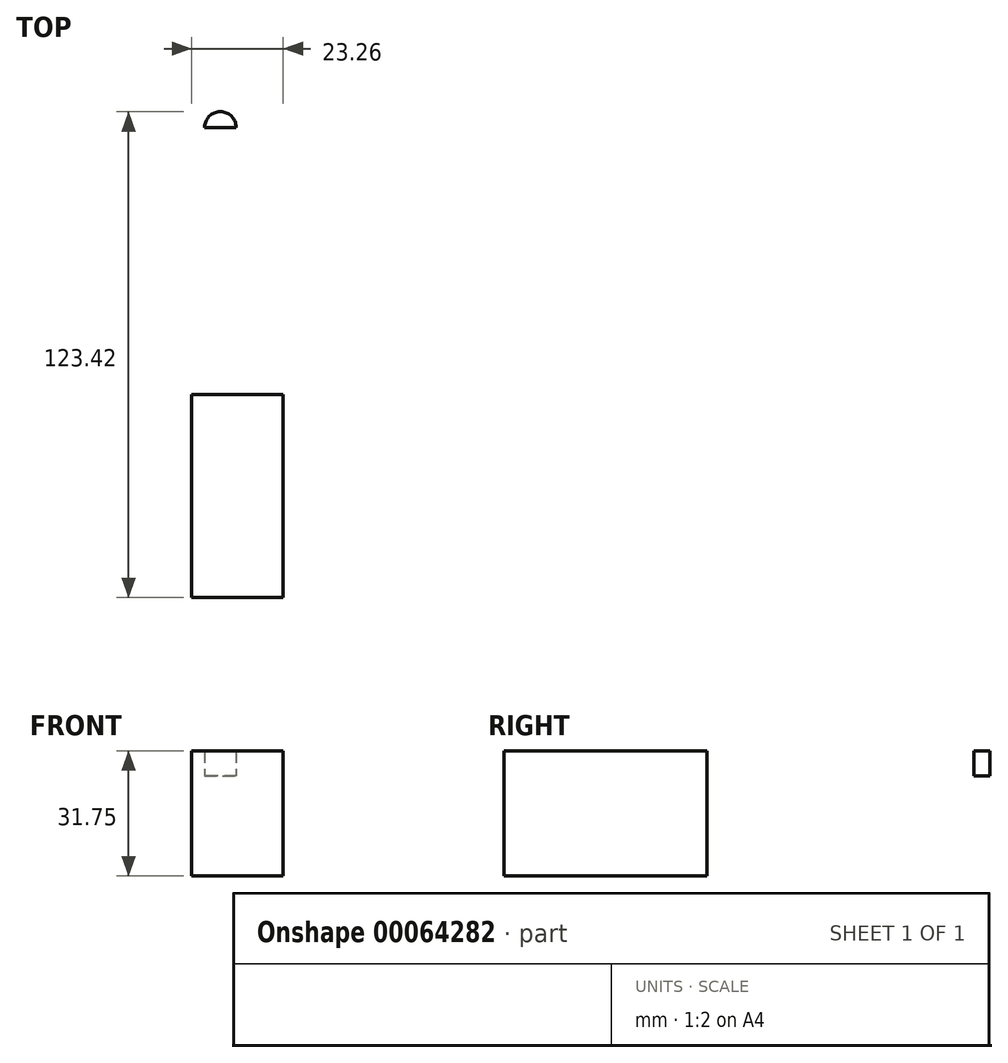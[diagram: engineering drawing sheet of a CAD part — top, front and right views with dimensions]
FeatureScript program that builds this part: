
annotation { "Feature Type Name" : "Feature", "Feature Type Description" : "" }
export const myFeature = defineFeature(function(context is Context, id is Id, definition is map)
    precondition{}
    {
        {
            var Q0;
            Q0=qCreatedBy(makeId("Top.planeOp"),FACE);
            var sketch = newSketch(context, id + "F0", { "sketchPlane" : qUnion([Q0])});
            skLineSegment(sketch, "E0.bottom", {"start": v(-34.6, -75.35) * mm, "end": v(-18.96, -75.35) * mm});
            skLineSegment(sketch, "E0.top", {"start": v(-34.6, -23.79) * mm, "end": v(-18.96, -23.79) * mm});
            skLineSegment(sketch, "E0.left", {"start": v(-34.6, -75.35) * mm, "end": v(-34.6, -23.79) * mm});
            skLineSegment(sketch, "E0.right", {"start": v(-18.96, -75.35) * mm, "end": v(-18.96, -23.79) * mm});
            skLineSegment(sketch, "E1.bottom", {"start": v(-31.27, -23.79) * mm, "end": v(-23.29, -23.79) * mm});
            skLineSegment(sketch, "E1.top", {"start": v(-31.27, 44.08) * mm, "end": v(-23.29, 44.08) * mm});
            skLineSegment(sketch, "E1.left", {"start": v(-31.27, -23.79) * mm, "end": v(-31.27, 44.08) * mm});
            skLineSegment(sketch, "E1.right", {"start": v(-23.29, -23.79) * mm, "end": v(-23.29, 44.08) * mm});
            skArc(sketch, "E2", {"start": v(-23.29, 44.08) * mm, "mid": v(-27.28, 48.07) * mm, "end": v(-31.27, 44.08) * mm});
            skSolve(sketch);
        }
        {
            var Q0;
            Q0=makeQuery(id+"F0.imprint","IMPRINT",FACE,{"disambiguationData":[TD([[makeQuery(id+"F0.imprint","IMPRINT",EDGE,{"derivedFrom":sQuery(id+"F0.wireOp",EDGE,"E1.bottom")}),1.0]])]});
            var Q1;
            Q1=makeQuery(id+"F0.imprint","IMPRINT",FACE,{"disambiguationData":[TD([[makeQuery(id+"F0.imprint","IMPRINT",EDGE,{"derivedFrom":sQuery(id+"F0.wireOp",EDGE,"E1.top")}),1.0]])]});
            var Q2;
            Q2=makeQuery(id+"F0.imprint","IMPRINT",FACE,{"disambiguationData":[TD([[makeQuery(id+"F0.imprint","IMPRINT",EDGE,{"derivedFrom":sQuery(id+"F0.wireOp",EDGE,"E0.bottom")}),1.0]])]});
            extrude(context, id + "F1", {"entities" : qUnion([Q0, Q1, Q2]), "depth" : 6.35 * mm});
        }
        {
            var Q0;
            Q0=makeQuery(id+"F1.opExtrude","SWEPT_FACE",FACE,{"disambiguationData":[OSD([sQuery(id+"F0.wireOp",EDGE,"E0.right")])]});
            extrude(context, id + "F2", {"entities" : qUnion([Q0]), "operationType" : NewBodyOperationType.ADD, "depth" : 7.62 * mm});
        }
        {
            var Q0;
            {var subQ0=sQuery(id+"F0.wireOp",EDGE,"E0.right");Q0=makeQuery(id+"F2.boolean.opBoolean","MERGE",FACE,{"derivedFrom":[makeQuery(id+"F1.opExtrude","CAP_FACE",FACE,{"disambiguationData":[OSD([sQuery(id+"F0.wireOp",EDGE,"E0.bottom"),sQuery(id+"F0.wireOp",EDGE,"E0.top"),sQuery(id+"F0.wireOp",EDGE,"E0.left"),subQ0,sQuery(id+"F0.wireOp",EDGE,"E1.left"),sQuery(id+"F0.wireOp",EDGE,"E1.right"),sQuery(id+"F0.wireOp",EDGE,"E2")])],"isStart":true}),makeQuery(id+"F2.opExtrude","SWEPT_FACE",FACE,{"disambiguationData":[OSD([subQ0]),TDD([makeQuery(id+"F1.opExtrude","CAP_EDGE",EDGE,{"disambiguationData":[OSD([subQ0])],"isStart":true})])]})]});}
            extrude(context, id + "F3", {"entities" : qUnion([Q0]), "operationType" : NewBodyOperationType.ADD, "depth" : 25.4 * mm});
        }
    });
